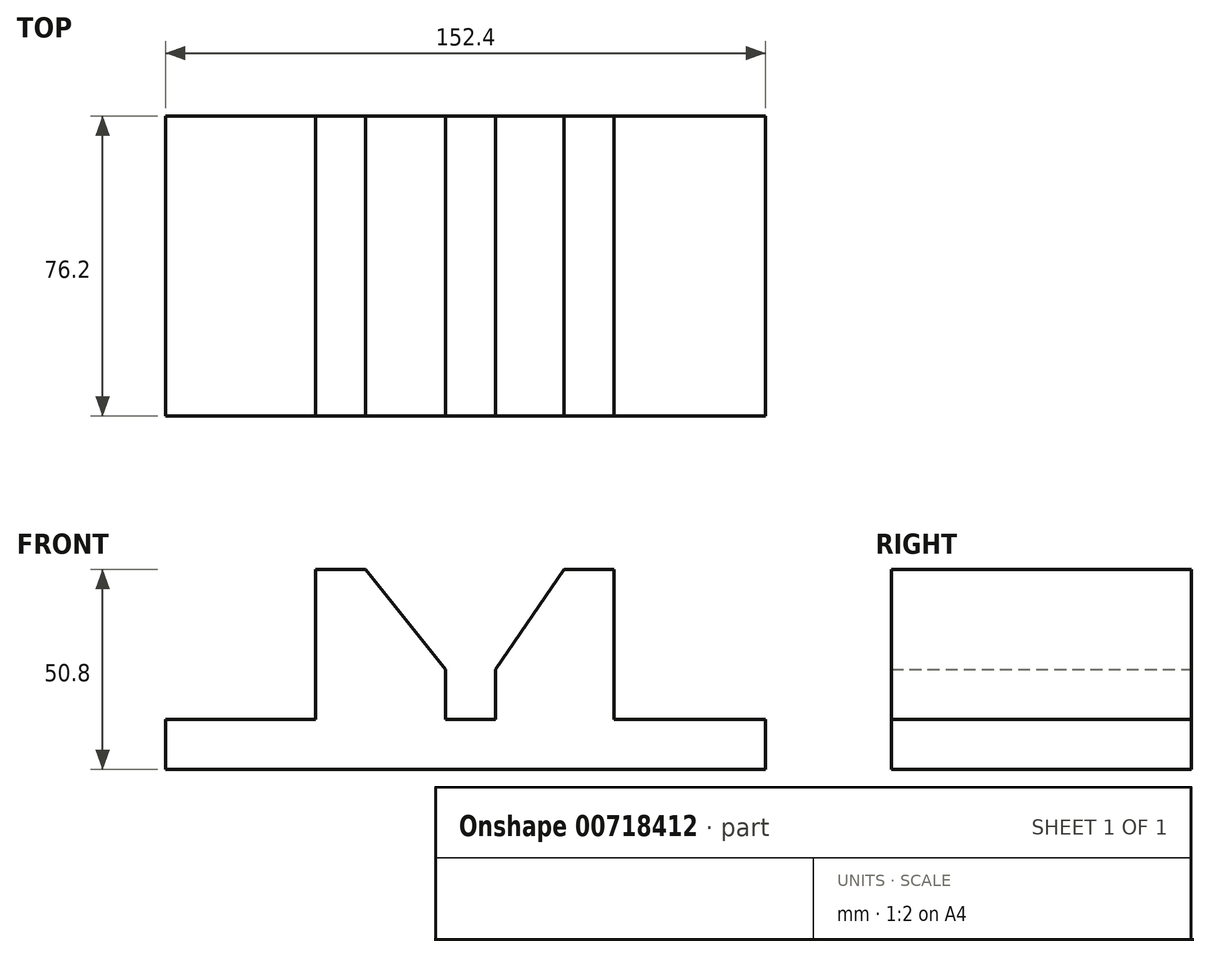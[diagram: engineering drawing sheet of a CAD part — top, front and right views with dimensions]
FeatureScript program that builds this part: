
annotation { "Feature Type Name" : "Feature", "Feature Type Description" : "" }
export const myFeature = defineFeature(function(context is Context, id is Id, definition is map)
    precondition{}
    {
        {
            var Q0;
            Q0=qCreatedBy(makeId("Front.planeOp"),FACE);
            var sketch = newSketch(context, id + "F0", { "sketchPlane" : qUnion([Q0])});
            skLineSegment(sketch, "E0", {"start": v(-73.47, -61.9) * mm, "end": v(78.93, -61.9) * mm});
            skLineSegment(sketch, "E1", {"start": v(78.93, -61.9) * mm, "end": v(78.93, -49.2) * mm});
            skLineSegment(sketch, "E2", {"start": v(40.47, -49.2) * mm, "end": v(78.93, -49.2) * mm});
            skLineSegment(sketch, "E3", {"start": v(40.47, -49.2) * mm, "end": v(40.47, -11.1) * mm});
            skLineSegment(sketch, "E4", {"start": v(40.47, -11.1) * mm, "end": v(27.77, -11.1) * mm});
            skLineSegment(sketch, "E5", {"start": v(27.77, -11.1) * mm, "end": v(10.35, -36.5) * mm});
            skLineSegment(sketch, "E6", {"start": v(10.35, -36.5) * mm, "end": v(10.35, -49.2) * mm});
            skLineSegment(sketch, "E7", {"start": v(10.35, -49.2) * mm, "end": v(-2.35, -49.2) * mm});
            skLineSegment(sketch, "E8", {"start": v(-2.35, -49.2) * mm, "end": v(-2.35, -36.5) * mm});
            skLineSegment(sketch, "E9", {"start": v(-2.35, -36.5) * mm, "end": v(-22.67, -11.1) * mm});
            skLineSegment(sketch, "E10", {"start": v(-22.67, -11.1) * mm, "end": v(-35.37, -11.1) * mm});
            skLineSegment(sketch, "E11", {"start": v(-35.37, -11.1) * mm, "end": v(-35.37, -49.2) * mm});
            skLineSegment(sketch, "E12", {"start": v(-35.37, -49.2) * mm, "end": v(-73.47, -49.2) * mm});
            skLineSegment(sketch, "E13", {"start": v(-73.47, -49.2) * mm, "end": v(-73.47, -61.9) * mm});
            skSolve(sketch);
        }
        {
            var Q0;
            Q0=makeQuery(id+"F0.imprint","IMPRINT",FACE,{"disambiguationData":[TD([[makeQuery(id+"F0.imprint","IMPRINT",EDGE,{"derivedFrom":sQuery(id+"F0.wireOp",EDGE,"E0")}),1.0]])]});
            extrude(context, id + "F1", {"entities" : qUnion([Q0]), "depth" : 76.2 * mm, "offsetDistance" : 25.4 * mm});
        }
    });
